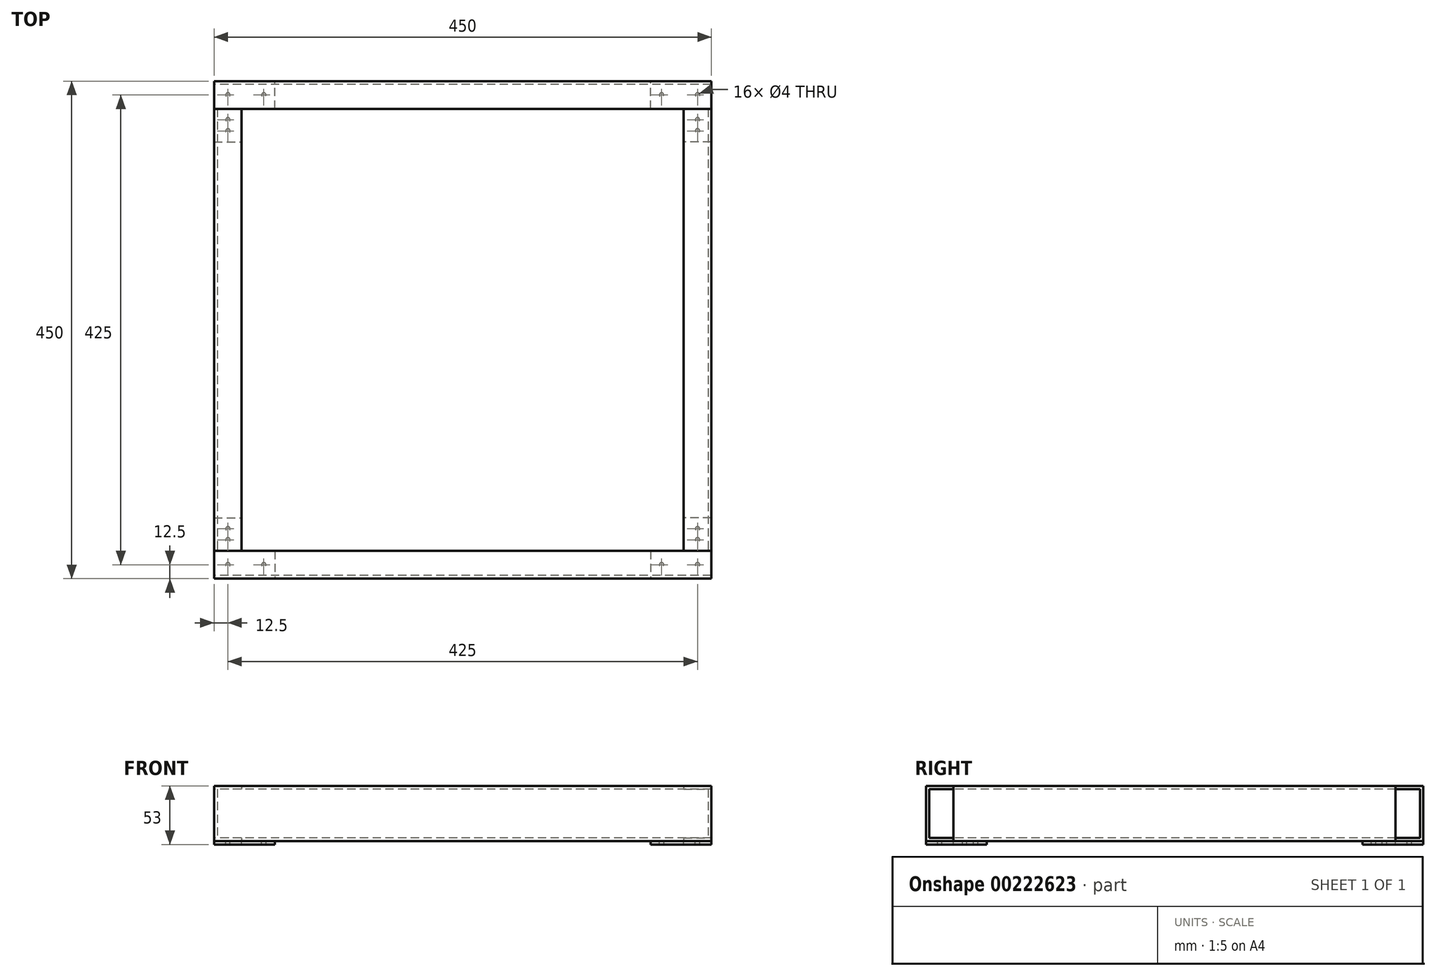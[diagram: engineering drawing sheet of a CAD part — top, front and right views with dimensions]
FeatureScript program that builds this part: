
annotation { "Feature Type Name" : "Feature", "Feature Type Description" : "" }
export const myFeature = defineFeature(function(context is Context, id is Id, definition is map)
    precondition{}
    {
        {
            var Q0;
            Q0=qCreatedBy(makeId("Top.planeOp"),FACE);
            var sketch = newSketch(context, id + "F0", { "sketchPlane" : qUnion([Q0])});
            skLineSegment(sketch, "E0.bottom", {"start": v(225, -225) * mm, "end": v(-225, -225) * mm});
            skLineSegment(sketch, "E0.top", {"start": v(225, 225) * mm, "end": v(-225, 225) * mm});
            skLineSegment(sketch, "E0.left", {"start": v(225, -225) * mm, "end": v(225, 225) * mm});
            skLineSegment(sketch, "E0.right", {"start": v(-225, -225) * mm, "end": v(-225, 225) * mm});
            skPoint(sketch, "E0.middle", {"position": v(0, 0) * mm});
            skLineSegment(sketch, "E1.bottom", {"start": v(200, -200) * mm, "end": v(-200, -200) * mm});
            skLineSegment(sketch, "E1.top", {"start": v(200, 200) * mm, "end": v(-200, 200) * mm});
            skLineSegment(sketch, "E1.left", {"start": v(200, -200) * mm, "end": v(200, 200) * mm});
            skLineSegment(sketch, "E1.right", {"start": v(-200, -200) * mm, "end": v(-200, 200) * mm});
            skLineSegment(sketch, "E2", {"start": v(-200, 200) * mm, "end": v(-225, 200) * mm});
            skLineSegment(sketch, "E3", {"start": v(200, 200) * mm, "end": v(225, 200) * mm});
            skLineSegment(sketch, "E4", {"start": v(-200, -200) * mm, "end": v(-225, -200) * mm});
            skLineSegment(sketch, "E5", {"start": v(200, -200) * mm, "end": v(225, -200) * mm});
            skSolve(sketch);
        }
        {
            var Q0;
            Q0=makeQuery(id+"F0.imprint","IMPRINT",FACE,{"disambiguationData":[TD([[makeQuery(id+"F0.imprint","IMPRINT",EDGE,{"derivedFrom":sQuery(id+"F0.wireOp",EDGE,"E1.right")}),1.0]])]});
            extrude(context, id + "F1", {"entities" : qUnion([Q0]), "depth" : 50 * mm});
        }
        {
            var Q0;
            {var subQ1=sQuery(id+"F0.wireOp",EDGE,"E0.top");Q0=makeQuery(id+"F0.imprint","IMPRINT",FACE,{"disambiguationData":[TD([[makeQuery(id+"F0.imprint","IMPRINT",EDGE,{"derivedFrom":subQ1}),1.0]])]});}
            extrude(context, id + "F2", {"entities" : qUnion([Q0]), "depth" : 50 * mm});
        }
        {
            var Q0;
            Q0=makeQuery(id+"F2.opExtrude","SWEPT_FACE",FACE,{"disambiguationData":[OSD([sQuery(id+"F0.wireOp",EDGE,"E0.right")])]});
            var sketch = newSketch(context, id + "F3", { "sketchPlane" : qUnion([Q0])});
            skLineSegment(sketch, "E6.bottom", {"start": v(-200, 47) * mm, "end": v(-222, 47) * mm});
            skLineSegment(sketch, "E6.top", {"start": v(-200, 3) * mm, "end": v(-222, 3) * mm});
            skLineSegment(sketch, "E6.left", {"start": v(-200, 47) * mm, "end": v(-200, 3) * mm});
            skLineSegment(sketch, "E6.right", {"start": v(-222, 47) * mm, "end": v(-222, 3) * mm});
            skLineSegment(sketch, "E7", {"start": v(-215.1, 47) * mm, "end": v(-215.1, 50) * mm, "construction": true});
            skLineSegment(sketch, "E8", {"start": v(-211, 3) * mm, "end": v(-211, 0) * mm, "construction": true});
            skLineSegment(sketch, "E9", {"start": v(-222, 29.53) * mm, "end": v(-225, 29.53) * mm, "construction": true});
            skSolve(sketch);
        }
        {
            var Q0;
            Q0=qSketchRegion(id+"F3",true);
            var Q1;
            Q1=makeQuery(id+"F2.opExtrude","SWEPT_FACE",FACE,{"disambiguationData":[OSD([sQuery(id+"F0.wireOp",EDGE,"E0.left")])]});
            extrude(context, id + "F4", {"entities" : qUnion([Q0]), "operationType" : NewBodyOperationType.REMOVE, "endBound" : BoundingType.UP_TO_SURFACE, "oppositeDirection" : true, "endBoundEntityFace" : qUnion([Q1]), "depth" : 25 * mm});
        }
        {
            var Q0;
            Q0=makeQuery(id+"F2.opExtrude","SWEPT_BODY",BODY,{"disambiguationData":[OSD([sQuery(id+"F0.wireOp",EDGE,"E0.top"),sQuery(id+"F0.wireOp",EDGE,"E0.left"),sQuery(id+"F0.wireOp",EDGE,"E0.right"),sQuery(id+"F0.wireOp",EDGE,"E1.top"),sQuery(id+"F0.wireOp",EDGE,"E2"),sQuery(id+"F0.wireOp",EDGE,"E3")])]});
            var Q1;
            Q1=qCreatedBy(makeId("Front.planeOp"),FACE);
            mirror(context, id + "F5", {"entities" : qUnion([Q0]), "mirrorPlane" : qUnion([Q1])});
        }
        {
            var Q0;
            Q0=makeQuery(id+"F1.opExtrude","SWEPT_FACE",FACE,{"disambiguationData":[OSD([sQuery(id+"F0.wireOp",EDGE,"E4")])]});
            var sketch = newSketch(context, id + "F6", { "sketchPlane" : qUnion([Q0])});
            skLineSegment(sketch, "E10.bottom", {"start": v(-200, 47) * mm, "end": v(-222, 47) * mm});
            skLineSegment(sketch, "E10.top", {"start": v(-200, 3) * mm, "end": v(-222, 3) * mm});
            skLineSegment(sketch, "E10.left", {"start": v(-200, 47) * mm, "end": v(-200, 3) * mm});
            skLineSegment(sketch, "E10.right", {"start": v(-222, 47) * mm, "end": v(-222, 3) * mm});
            skLineSegment(sketch, "E11", {"start": v(-211, 47) * mm, "end": v(-211, 50) * mm, "construction": true});
            skLineSegment(sketch, "E12", {"start": v(-222, 25) * mm, "end": v(-225, 25) * mm, "construction": true});
            skLineSegment(sketch, "E13", {"start": v(-211, 3) * mm, "end": v(-211, 0) * mm, "construction": true});
            skPoint(sketch, "E13.endSnap0", {"position": v(-212.5, 0) * mm});
            skSolve(sketch);
        }
        {
            var Q0;
            Q0=qSketchRegion(id+"F6",true);
            var Q1;
            Q1=makeQuery(id+"F1.opExtrude","SWEPT_FACE",FACE,{"disambiguationData":[OSD([sQuery(id+"F0.wireOp",EDGE,"E2")])]});
            extrude(context, id + "F7", {"entities" : qUnion([Q0]), "operationType" : NewBodyOperationType.REMOVE, "endBound" : BoundingType.UP_TO_SURFACE, "oppositeDirection" : true, "endBoundEntityFace" : qUnion([Q1]), "depth" : 25 * mm});
        }
        {
            var Q0;
            Q0=makeQuery(id+"F1.opExtrude","SWEPT_BODY",BODY,{"disambiguationData":[OSD([sQuery(id+"F0.wireOp",EDGE,"E0.right"),sQuery(id+"F0.wireOp",EDGE,"E1.right"),sQuery(id+"F0.wireOp",EDGE,"E2"),sQuery(id+"F0.wireOp",EDGE,"E4")])]});
            var Q1;
            Q1=qCreatedBy(makeId("Right.planeOp"),FACE);
            mirror(context, id + "F8", {"entities" : qUnion([Q0]), "mirrorPlane" : qUnion([Q1])});
        }
        {
            var Q0;
            Q0=makeQuery(id+"F5.opPattern","COPY",FACE,{"derivedFrom":makeQuery(id+"F2.opExtrude","CAP_FACE",FACE,{"disambiguationData":[OSD([sQuery(id+"F0.wireOp",EDGE,"E0.top"),sQuery(id+"F0.wireOp",EDGE,"E0.left"),sQuery(id+"F0.wireOp",EDGE,"E0.right"),sQuery(id+"F0.wireOp",EDGE,"E1.top"),sQuery(id+"F0.wireOp",EDGE,"E2"),sQuery(id+"F0.wireOp",EDGE,"E3")])],"isStart":true}),"instanceName":"1"});
            var sketch = newSketch(context, id + "F9", { "sketchPlane" : qUnion([Q0])});
            skLineSegment(sketch, "E14", {"start": v(-225, 225) * mm, "end": v(-225, 170) * mm});
            skLineSegment(sketch, "E15", {"start": v(-225, 170) * mm, "end": v(-200, 170) * mm});
            skLineSegment(sketch, "E16", {"start": v(-200, 170) * mm, "end": v(-200, 200) * mm});
            skLineSegment(sketch, "E17", {"start": v(-200, 200) * mm, "end": v(-170, 200) * mm});
            skLineSegment(sketch, "E18", {"start": v(-170, 200) * mm, "end": v(-170, 225) * mm});
            skLineSegment(sketch, "E19", {"start": v(-170, 225) * mm, "end": v(-225, 225) * mm});
            skLineSegment(sketch, "E20", {"start": v(-225, 212.5) * mm, "end": v(-170, 212.5) * mm, "construction": true});
            skLineSegment(sketch, "E21", {"start": v(-212.5, 170) * mm, "end": v(-212.5, 225) * mm, "construction": true});
            skCircle(sketch, "E22", {"center": v(-212.5, 212.5) * mm, "radius": 2 * mm});
            skCircle(sketch, "E23", {"center": v(-180, 212.5) * mm, "radius": 2 * mm});
            skCircle(sketch, "E24", {"center": v(-212.5, 180) * mm, "radius": 2 * mm});
            skCircle(sketch, "E25", {"center": v(-212.5, 190) * mm, "radius": 2 * mm});
            skSolve(sketch);
        }
        {
            var Q0;
            Q0=qSketchRegion(id+"F9",true);
            extrude(context, id + "F10", {"entities" : qUnion([Q0]), "depth" : 3 * mm});
        }
        {
            var Q0;
            Q0=makeQuery(id+"F10.opExtrude","SWEPT_BODY",BODY,{"disambiguationData":[OSD([sQuery(id+"F9.wireOp",EDGE,"E14"),sQuery(id+"F9.wireOp",EDGE,"E15"),sQuery(id+"F9.wireOp",EDGE,"E16"),sQuery(id+"F9.wireOp",EDGE,"E17"),sQuery(id+"F9.wireOp",EDGE,"E18"),sQuery(id+"F9.wireOp",EDGE,"E19"),sQuery(id+"F9.wireOp",EDGE,"E22"),sQuery(id+"F9.wireOp",EDGE,"E23"),sQuery(id+"F9.wireOp",EDGE,"E24"),sQuery(id+"F9.wireOp",EDGE,"E25")])]});
            var Q1;
            Q1=qCreatedBy(makeId("Front.planeOp"),FACE);
            mirror(context, id + "F11", {"entities" : qUnion([Q0]), "mirrorPlane" : qUnion([Q1])});
        }
        {
            var Q0;
            Q0=makeQuery(id+"F10.opExtrude","SWEPT_BODY",BODY,{"disambiguationData":[OSD([sQuery(id+"F9.wireOp",EDGE,"E14"),sQuery(id+"F9.wireOp",EDGE,"E15"),sQuery(id+"F9.wireOp",EDGE,"E16"),sQuery(id+"F9.wireOp",EDGE,"E17"),sQuery(id+"F9.wireOp",EDGE,"E18"),sQuery(id+"F9.wireOp",EDGE,"E19"),sQuery(id+"F9.wireOp",EDGE,"E22"),sQuery(id+"F9.wireOp",EDGE,"E23"),sQuery(id+"F9.wireOp",EDGE,"E24"),sQuery(id+"F9.wireOp",EDGE,"E25")])]});
            var Q1;
            Q1=makeQuery(id+"F11.opPattern","COPY",BODY,{"derivedFrom":makeQuery(id+"F10.opExtrude","SWEPT_BODY",BODY,{"disambiguationData":[OSD([sQuery(id+"F9.wireOp",EDGE,"E14"),sQuery(id+"F9.wireOp",EDGE,"E15"),sQuery(id+"F9.wireOp",EDGE,"E16"),sQuery(id+"F9.wireOp",EDGE,"E17"),sQuery(id+"F9.wireOp",EDGE,"E18"),sQuery(id+"F9.wireOp",EDGE,"E19"),sQuery(id+"F9.wireOp",EDGE,"E22"),sQuery(id+"F9.wireOp",EDGE,"E23"),sQuery(id+"F9.wireOp",EDGE,"E24"),sQuery(id+"F9.wireOp",EDGE,"E25")])]}),"instanceName":"1"});
            var Q2;
            Q2=qCreatedBy(makeId("Right.planeOp"),FACE);
            mirror(context, id + "F12", {"entities" : qUnion([Q0, Q1]), "mirrorPlane" : qUnion([Q2])});
        }
    });
